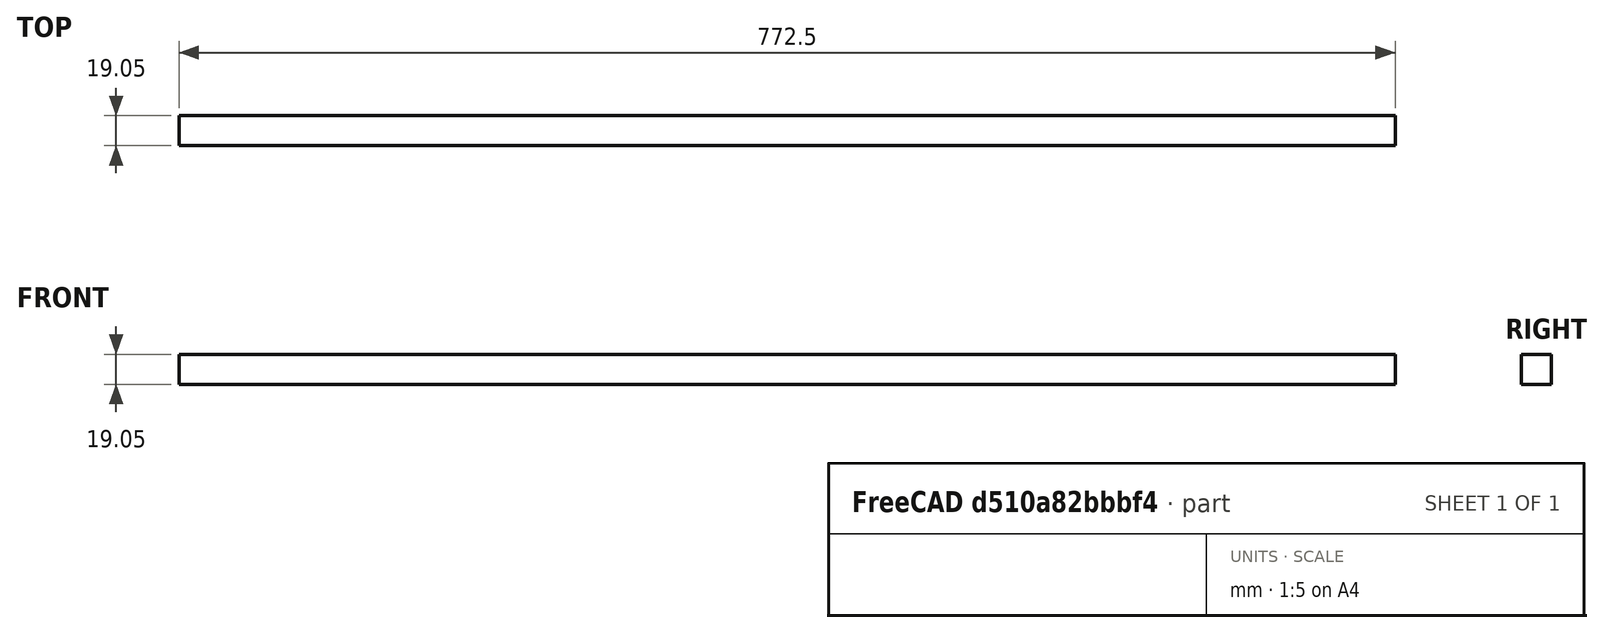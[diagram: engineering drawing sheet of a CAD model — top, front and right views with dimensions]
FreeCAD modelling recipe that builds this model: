
FCSTD DOCUMENT  (FreeCAD 0.20R29177 (Git))
Label: shortStringer
License: All rights reserved
LicenseURL: http://en.wikipedia.org/wiki/All_rights_reserved
objects: Sketcher::SketchObject×1, PartDesign::Pad×1, PartDesign::Body×1
note: 4 computed .brp shape members not serialized (recipe doc carries the construction recipe); baked Part::Feature solids carry a one-line shape summary decoded from their .brp

FEATURE [Sketcher::SketchObject] Sketch
  FullyConstrained = true
  MapMode = 5
  Support = -> [XY_Plane]
  expr: Constraints[10] = 801.55 - 5 - 5 - 3 / 4 * 25.4
  expr: Constraints[9] = 3 / 4 * 25.4
  sketch-geometry (4):
    g0: LineSegment StartX=0 StartY=0 StartZ=0 EndX=772.5 EndY=0 EndZ=0
    g1: LineSegment StartX=772.5 StartY=0 StartZ=0 EndX=772.5 EndY=19.05 EndZ=0
    g2: LineSegment StartX=772.5 StartY=19.05 StartZ=0 EndX=0 EndY=19.05 EndZ=0
    g3: LineSegment StartX=0 StartY=19.05 StartZ=0 EndX=0 EndY=0 EndZ=0
  constraints (11):
    c: Coincident(g0,g1)
    c: Coincident(g1,g2)
    c: Coincident(g2,g3)
    c: Coincident(g3,g0)
    c: Horizontal(g0)
    c: Horizontal(g2)
    c: Vertical(g1)
    c: Vertical(g3)
    c: Coincident(g0,g-1)
    c: DistanceY(g3,g3) = 19.05
    c: DistanceX(g0,g0) = 772.5
FEATURE [PartDesign::Pad] Pad
  Direction = (0,0,1)
  Length = 19.05
  Length2 = 10
  Profile = -> Sketch
  ReferenceAxis = -> Sketch [N_Axis]
  Type = 0
  expr: Length = 3 / 4 * 25.4
FEATURE [PartDesign::Body] Body
  Group = -> [Sketch,Pad]
  Origin = -> Origin
  Tip = -> Pad
